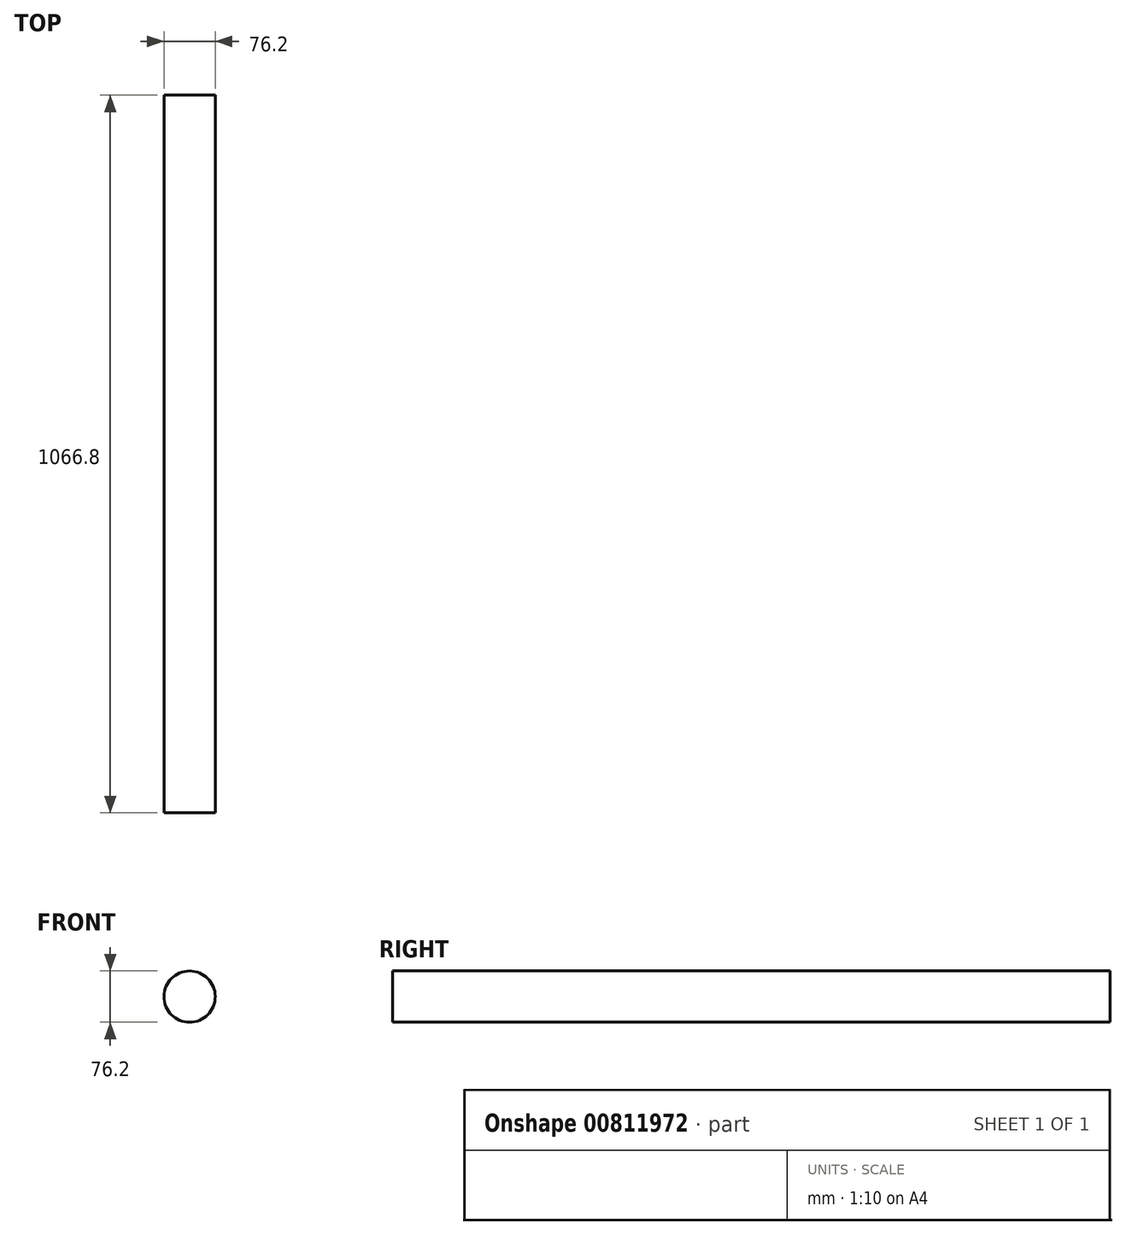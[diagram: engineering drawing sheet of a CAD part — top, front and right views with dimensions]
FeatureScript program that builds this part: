
annotation { "Feature Type Name" : "Feature", "Feature Type Description" : "" }
export const myFeature = defineFeature(function(context is Context, id is Id, definition is map)
    precondition{}
    {
        {
            var Q0;
            Q0=qCreatedBy(makeId("Front.planeOp"),FACE);
            var sketch = newSketch(context, id + "F0", { "sketchPlane" : qUnion([Q0])});
            skCircle(sketch, "E0", {"center": v(0, 0) * mm, "radius": 38.1 * mm});
            skSolve(sketch);
        }
        {
            var Q0;
            Q0=makeQuery(id+"F0.imprint","IMPRINT",FACE,{"disambiguationData":[TD([[makeQuery(id+"F0.imprint","IMPRINT",EDGE,{"derivedFrom":sQuery(id+"F0.wireOp",EDGE,"E0")}),1.0]])]});
            extrude(context, id + "F1", {"entities" : qUnion([Q0]), "endBound" : BoundingType.SYMMETRIC, "depth" : 1066.8 * mm, "offsetDistance" : 25.4 * mm});
        }
    });
